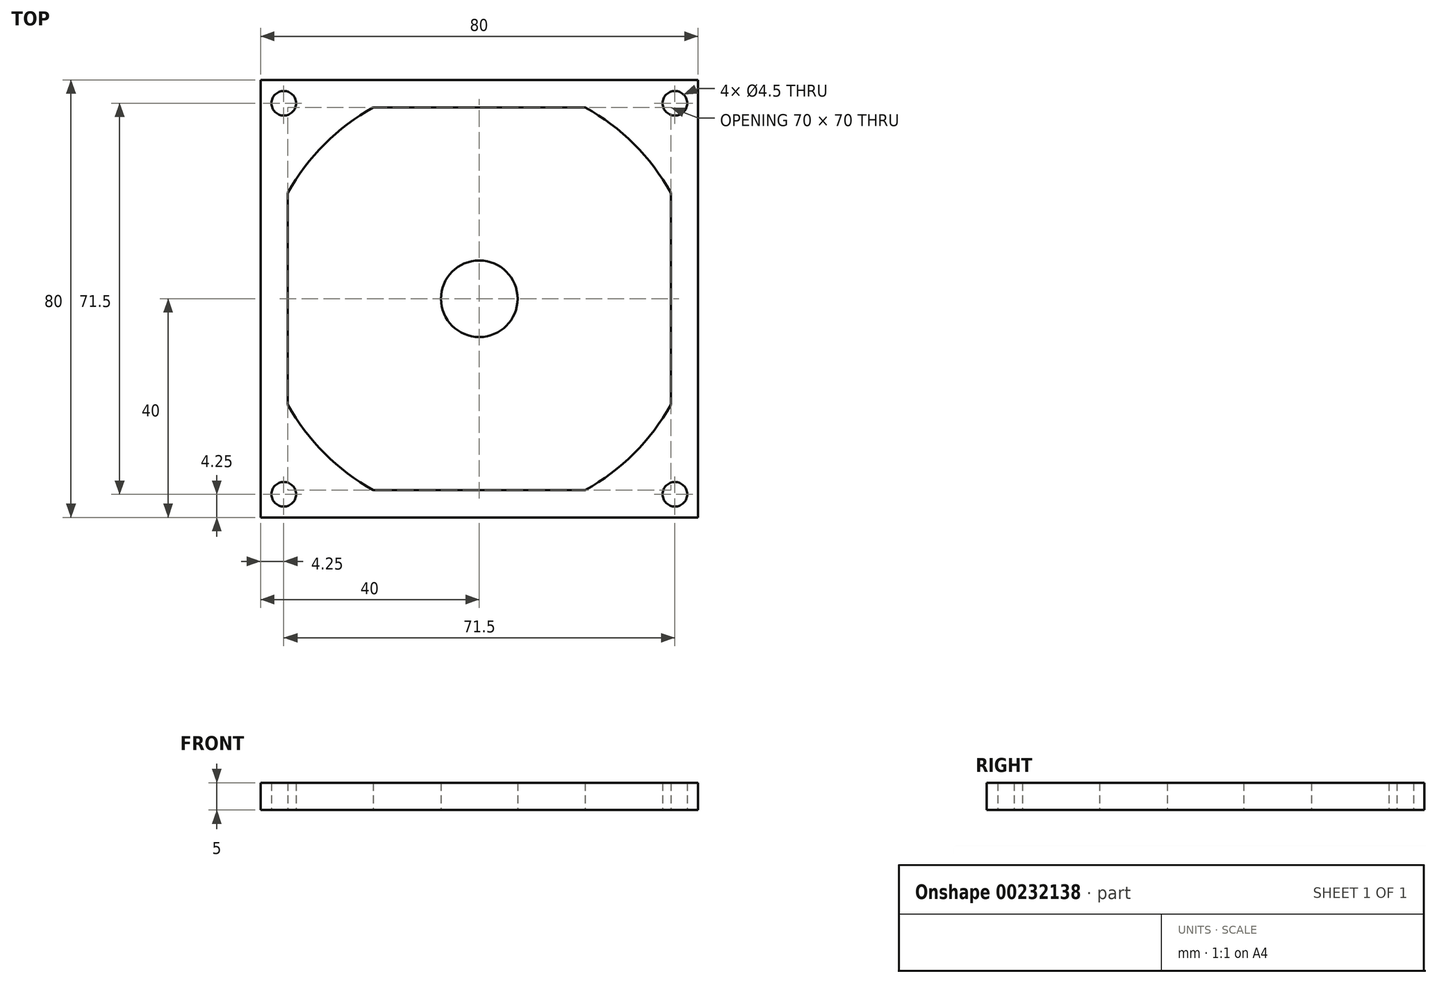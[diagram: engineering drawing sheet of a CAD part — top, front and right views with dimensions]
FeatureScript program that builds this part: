
annotation { "Feature Type Name" : "Feature", "Feature Type Description" : "" }
export const myFeature = defineFeature(function(context is Context, id is Id, definition is map)
    precondition{}
    {
        {
            var Q0;
            Q0=qCreatedBy(makeId("Top.planeOp"),FACE);
            var sketch = newSketch(context, id + "F0", { "sketchPlane" : qUnion([Q0])});
            skArc(sketch, "E0", {"start": v(-35, -19.36) * mm, "mid": v(-28.28, -28.28) * mm, "end": v(-19.36, -35) * mm});
            skLineSegment(sketch, "E1.bottom", {"start": v(19.36, 35) * mm, "end": v(-19.36, 35) * mm});
            skLineSegment(sketch, "E1.top", {"start": v(19.36, -35) * mm, "end": v(-19.36, -35) * mm});
            skLineSegment(sketch, "E1.left", {"start": v(35, 19.36) * mm, "end": v(35, -19.36) * mm});
            skLineSegment(sketch, "E1.right", {"start": v(-35, 19.36) * mm, "end": v(-35, -19.36) * mm});
            skArc(sketch, "E2.trimOffspring", {"start": v(-19.36, 35) * mm, "mid": v(-28.28, 28.28) * mm, "end": v(-35, 19.36) * mm});
            skArc(sketch, "E3.trimOffspring", {"start": v(35, 19.36) * mm, "mid": v(28.28, 28.28) * mm, "end": v(19.36, 35) * mm});
            skArc(sketch, "E4.trimOffspring", {"start": v(19.36, -35) * mm, "mid": v(28.28, -28.28) * mm, "end": v(35, -19.36) * mm});
            skLineSegment(sketch, "E5.bottom", {"start": v(40, 40) * mm, "end": v(-40, 40) * mm});
            skLineSegment(sketch, "E5.top", {"start": v(40, -40) * mm, "end": v(-40, -40) * mm});
            skLineSegment(sketch, "E5.left", {"start": v(40, 40) * mm, "end": v(40, -40) * mm});
            skLineSegment(sketch, "E5.right", {"start": v(-40, 40) * mm, "end": v(-40, -40) * mm});
            skCircle(sketch, "E6", {"center": v(35.75, 35.75) * mm, "radius": 2.25 * mm});
            skCircle(sketch, "E7.MirrorC", {"center": v(-35.75, 35.75) * mm, "radius": 2.25 * mm});
            skCircle(sketch, "E8.MirrorC", {"center": v(-35.75, -35.75) * mm, "radius": 2.25 * mm});
            skCircle(sketch, "E9.MirrorC", {"center": v(35.75, -35.75) * mm, "radius": 2.25 * mm});
            skCircle(sketch, "E10", {"center": v(0, 0) * mm, "radius": 7 * mm});
            skSolve(sketch);
        }
        {
            var Q0;
            Q0=makeQuery(id+"F0.imprint","IMPRINT",FACE,{"disambiguationData":[TD([[makeQuery(id+"F0.imprint","IMPRINT",EDGE,{"derivedFrom":sQuery(id+"F0.wireOp",EDGE,"E0")}),-1.0]])]});
            var Q1;
            Q1=makeQuery(id+"F0.imprint","IMPRINT",FACE,{"disambiguationData":[TD([[makeQuery(id+"F0.imprint","IMPRINT",EDGE,{"derivedFrom":sQuery(id+"F0.wireOp",EDGE,"E10")}),1.0]])]});
            extrude(context, id + "F1", {"entities" : qUnion([Q0, Q1]), "depth" : 5 * mm});
        }
        {
            var Q0;
            Q0=qCreatedBy(makeId("Top.planeOp"),FACE);
            cPlane(context, id + "F2", {"entities" : qUnion([Q0]), "cplaneType" : CPlaneType.OFFSET, "offset" : 2.5 * mm, "width" : 150 * mm, "height" : 150 * mm});
        }
    });
